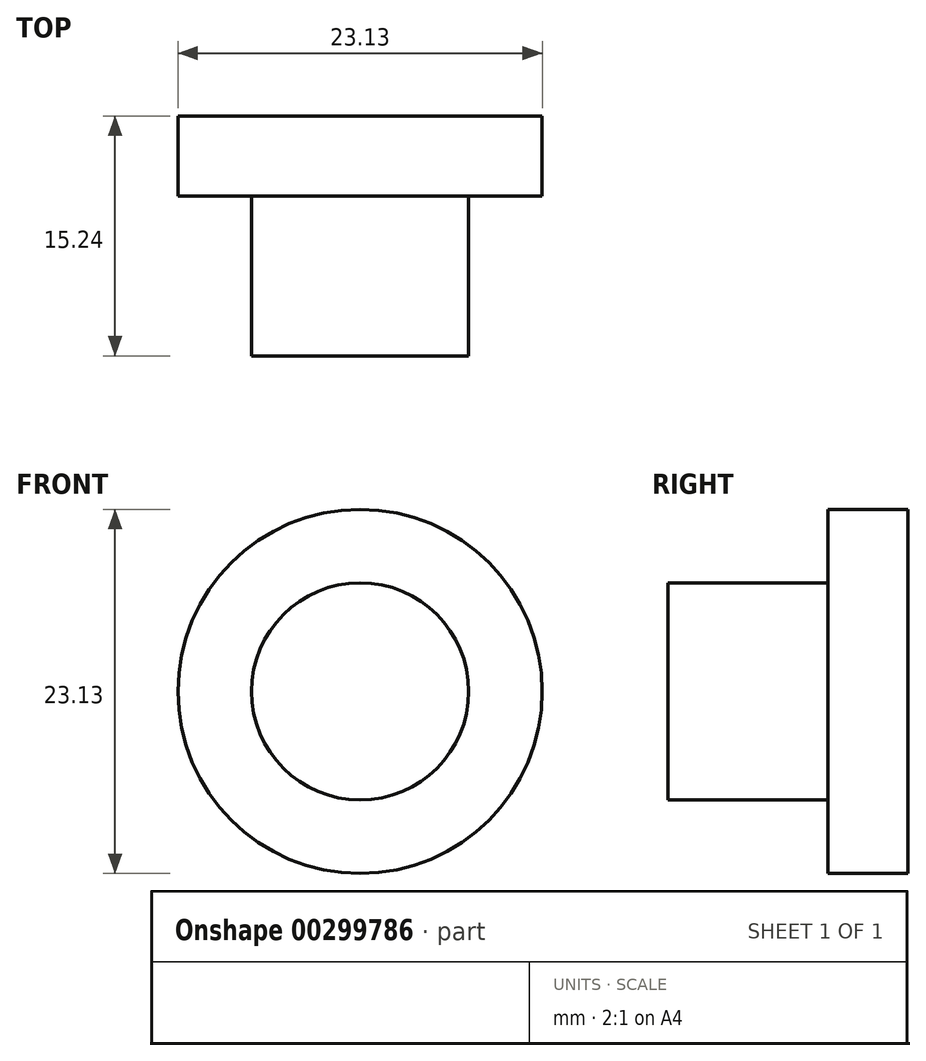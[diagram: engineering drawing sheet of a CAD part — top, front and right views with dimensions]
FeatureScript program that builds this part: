
annotation { "Feature Type Name" : "Feature", "Feature Type Description" : "" }
export const myFeature = defineFeature(function(context is Context, id is Id, definition is map)
    precondition{}
    {
        {
            var Q0;
            Q0=qCreatedBy(makeId("Front.planeOp"),FACE);
            var sketch = newSketch(context, id + "F0", { "sketchPlane" : qUnion([Q0])});
            skCircle(sketch, "E0", {"center": v(-44.54, 34.49) * mm, "radius": 11.57 * mm});
            skSolve(sketch);
        }
        {
            var Q0;
            Q0=makeQuery(id+"F0.imprint","IMPRINT",FACE,{"disambiguationData":[TD([[makeQuery(id+"F0.imprint","IMPRINT",EDGE,{"derivedFrom":sQuery(id+"F0.wireOp",EDGE,"E0")}),1.0]])]});
            extrude(context, id + "F1", {"entities" : qUnion([Q0]), "depth" : 5.08 * mm});
        }
        {
            var Q0;
            Q0=makeQuery(id+"F1.opExtrude","CAP_FACE",FACE,{"disambiguationData":[OSD([sQuery(id+"F0.wireOp",EDGE,"E0")])],"isStart":false});
            var sketch = newSketch(context, id + "F2", { "sketchPlane" : qUnion([Q0])});
            skCircle(sketch, "E1", {"center": v(-44.54, 34.49) * mm, "radius": 6.5 * mm});
            skSolve(sketch);
        }
        {
            var Q0;
            Q0=makeQuery(id+"F2.imprint","IMPRINT",FACE,{"disambiguationData":[TD([[makeQuery(id+"F2.imprint","IMPRINT",EDGE,{"derivedFrom":sQuery(id+"F2.wireOp",EDGE,"E1")}),1.0]])]});
            extrude(context, id + "F3", {"entities" : qUnion([Q0]), "operationType" : NewBodyOperationType.REMOVE, "oppositeDirection" : true, "depth" : 2.54 * mm});
        }
        {
            var Q0;
            Q0=makeQuery(id+"F3.boolean.opBoolean","COPY",FACE,{"derivedFrom":makeQuery(id+"F3.opExtrude","CAP_FACE",FACE,{"disambiguationData":[OSD([sQuery(id+"F2.wireOp",EDGE,"E1")])],"isStart":false})});
            var sketch = newSketch(context, id + "F4", { "sketchPlane" : qUnion([Q0])});
            skCircle(sketch, "E2", {"center": v(-44.54, 34.49) * mm, "radius": 6.9 * mm});
            skSolve(sketch);
        }
        {
            var Q0;
            Q0 = qSketchRegion(id + "F4", true);
            extrude(context, id + "F5", {"entities" : qUnion([Q0]), "operationType" : NewBodyOperationType.ADD, "depth" : 12.7 * mm});
        }
    });
